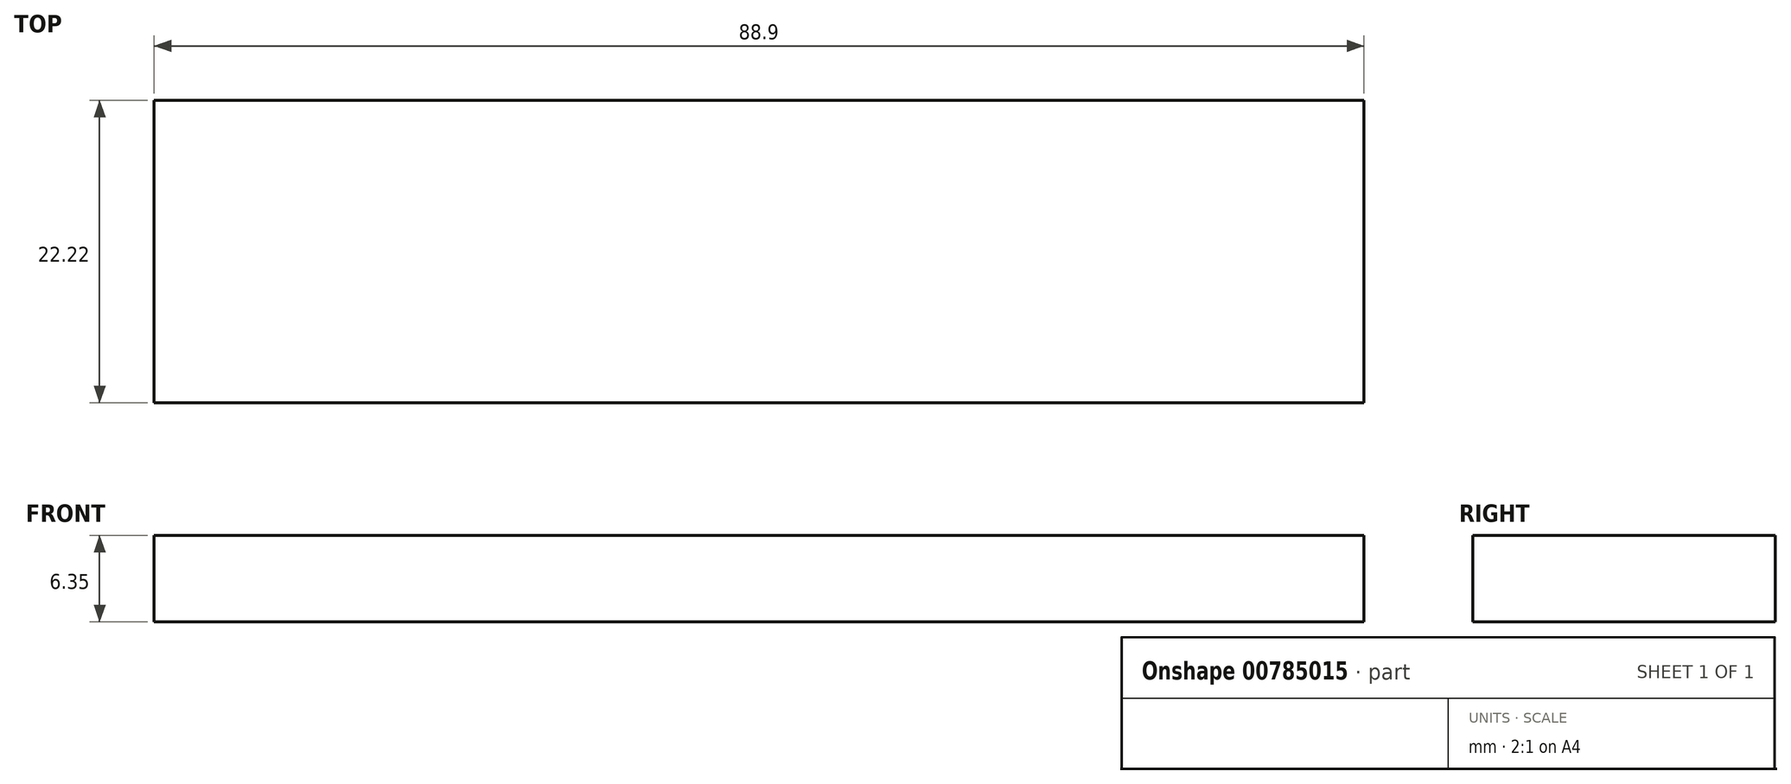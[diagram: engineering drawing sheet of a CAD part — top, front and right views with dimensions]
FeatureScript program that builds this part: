
annotation { "Feature Type Name" : "Feature", "Feature Type Description" : "" }
export const myFeature = defineFeature(function(context is Context, id is Id, definition is map)
    precondition{}
    {
        {
            var Q0;
            Q0=qCreatedBy(makeId("Top.planeOp"),FACE);
            var sketch = newSketch(context, id + "F0", { "sketchPlane" : qUnion([Q0])});
            skLineSegment(sketch, "E0.bottom", {"start": v(44.45, 11.11) * mm, "end": v(-44.45, 11.11) * mm});
            skLineSegment(sketch, "E0.top", {"start": v(44.45, -11.11) * mm, "end": v(-44.45, -11.11) * mm});
            skLineSegment(sketch, "E0.left", {"start": v(44.45, 11.11) * mm, "end": v(44.45, -11.11) * mm});
            skLineSegment(sketch, "E0.right", {"start": v(-44.45, 11.11) * mm, "end": v(-44.45, -11.11) * mm});
            skPoint(sketch, "E0.middle", {"position": v(0, 0) * mm});
            skSolve(sketch);
        }
        {
            var Q0;
            Q0 = qSketchRegion(id + "F0", true);
            extrude(context, id + "F1", {"entities" : qUnion([Q0]), "depth" : 6.35 * mm, "offsetDistance" : 25.4 * mm});
        }
    });
